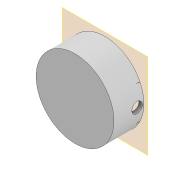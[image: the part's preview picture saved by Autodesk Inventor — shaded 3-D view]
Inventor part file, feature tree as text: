
AUTODESK INVENTOR PART (.ipt)
format: ipt  version: 2022 (Build 260153000, 153)  size: 1,001,472 bytes
history: native  units: mm
features: extrude x7, sketch x7, other x6, reference x4, projected_geometry x4, plane x2
ambient origin geometry x8: Origin, YZ Plane, XZ Plane, XY Plane, X Axis, Y Axis, Z Axis, Center Point
bodies: Volumenkörper1 (feature_tree)
feature tree (30):
  plane  "Arbeitsebene1"
  extrude  "Extrusion1"  Depth=18.0mm TaperAngle=0.0deg
  extrude  "Extrusion2"  Depth=18.0mm TaperAngle=0.0deg
  sketch  "Skizze3"  dims[d7=10.0mm d8=0.0mm d9=0.5mm]
  plane  "Arbeitsebene2"
  extrude  "Extrusion3"  Depth=10.0mm
  extrude  "Extrusion4"  TaperAngle=180.0deg  [1 undecoded]
  extrude  "Extrusion5"  Depth=7.0mm
  extrude  "Extrusion6"  [1 undecoded]
  extrude  "Extrusion7"  [1 undecoded]
  sketch  "Skizze1"  dims[d0=2.0mm d1=18.0mm d2=0.0mm]
  reference  "Referenz1"
  sketch  "Skizze2"  dims[d3=2.0mm d4=0.0mm d5=18.0mm d6=0.0mm]
  reference  "Referenz2"
  sketch  "Skizze4"  dims[d10=4.3mm d11=0.0mm d18=180.0deg]
  reference  "Referenz3"
  projected_geometry  "Projizierte Kontur1"
  projected_geometry  "Projizierte Kontur2"
  projected_geometry  "Projizierte Kontur3"
  projected_geometry  "Projizierte Kontur4"
  sketch  "Skizze5"  dims[d19=23.0mm d20=0.0mm d21=7.0mm]
  reference  "Referenz4"
  sketch  "Skizze7"  dims[d22=23.0mm d23=0.0mm]
  sketch  "Skizze8"
  other  "Planktoscope_Mini_v0.iam"
  other  "Planktoscope_Mini_Peristalticpump:1"
  other  "Pump_Base_Motor:1"
  other  "Planktoscope_Mini_Electronicbase.iam"
  other  "00_ULN2003 Stepper Driver:1"
  other  "00_Wemos-Mini-D1-ESP32:1"
note: 3 required parameter values undecoded (feature->parameter linkage not recoverable at this tier; creation-order binding heuristic only, values carry confidence <= 0.55)
